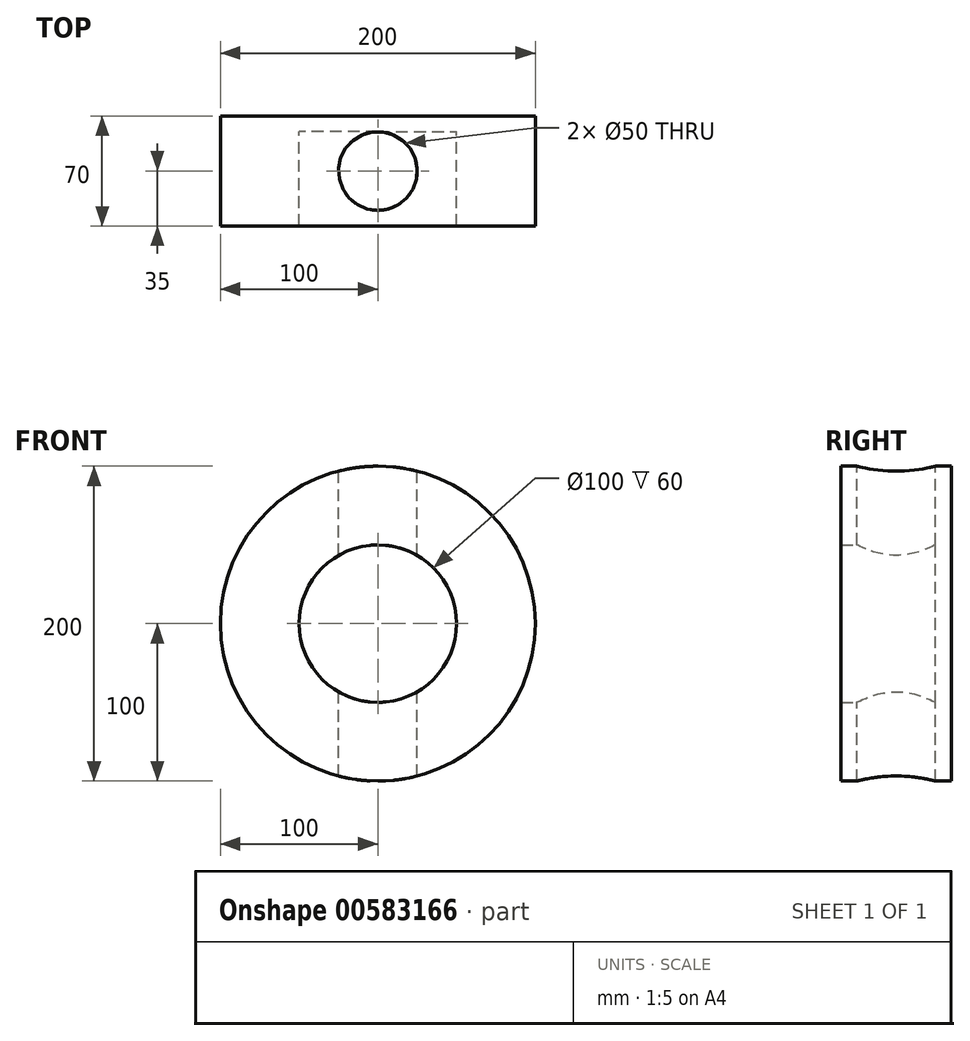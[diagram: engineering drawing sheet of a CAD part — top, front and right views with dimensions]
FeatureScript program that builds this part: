
annotation { "Feature Type Name" : "Feature", "Feature Type Description" : "" }
export const myFeature = defineFeature(function(context is Context, id is Id, definition is map)
    precondition{}
    {
        {
            var Q0;
            Q0=qCreatedBy(makeId("Front.planeOp"),FACE);
            var sketch = newSketch(context, id + "F0", { "sketchPlane" : qUnion([Q0])});
            skCircle(sketch, "E0", {"center": v(0, 0) * mm, "radius": 100 * mm});
            skCircle(sketch, "E1", {"center": v(0, 0) * mm, "radius": 50 * mm});
            skSolve(sketch);
        }
        {
            var Q0;
            Q0=makeQuery(id+"F0.imprint","IMPRINT",FACE,{"disambiguationData":[TD([[makeQuery(id+"F0.imprint","IMPRINT",EDGE,{"derivedFrom":sQuery(id+"F0.wireOp",EDGE,"E0")}),1.0]])]});
            extrude(context, id + "F1", {"entities" : qUnion([Q0]), "depth" : 60 * mm, "offsetDistance" : 25 * mm});
        }
        {
            var Q0;
            Q0=qCreatedBy(makeId("Top.planeOp"),FACE);
            var sketch = newSketch(context, id + "F2", { "sketchPlane" : qUnion([Q0])});
            skCircle(sketch, "E2", {"center": v(0, -25) * mm, "radius": 25 * mm});
            skSolve(sketch);
        }
        {
            var Q0;
            Q0=makeQuery(id+"F1.opExtrude","CAP_FACE",FACE,{"disambiguationData":[OSD([sQuery(id+"F0.wireOp",EDGE,"E0"),sQuery(id+"F0.wireOp",EDGE,"E1")])],"isStart":true});
            var sketch = newSketch(context, id + "F3", { "sketchPlane" : qUnion([Q0])});
            skCircle(sketch, "E3", {"center": v(0, 0) * mm, "radius": 100 * mm});
            skSolve(sketch);
        }
        {
            var Q0;
            Q0 = qSketchRegion(id + "F3", true);
            extrude(context, id + "F4", {"entities" : qUnion([Q0]), "operationType" : NewBodyOperationType.ADD, "depth" : 10 * mm, "offsetDistance" : 25 * mm});
        }
        {
            var Q0;
            Q0=makeQuery(id+"F2.imprint","IMPRINT",FACE,{"disambiguationData":[TD([[makeQuery(id+"F2.imprint","IMPRINT",EDGE,{"derivedFrom":sQuery(id+"F2.wireOp",EDGE,"E2")}),1.0]])]});
            extrude(context, id + "F5", {"entities" : qUnion([Q0]), "operationType" : NewBodyOperationType.REMOVE, "endBound" : BoundingType.THROUGH_ALL, "oppositeDirection" : true, "depth" : 25 * mm, "offsetDistance" : 25 * mm, "hasSecondDirection" : true, "secondDirectionBound" : SecondDirectionBoundingType.THROUGH_ALL, "secondDirectionOppositeDirection" : false, "secondDirectionDepth" : 25 * mm});
        }
    });
